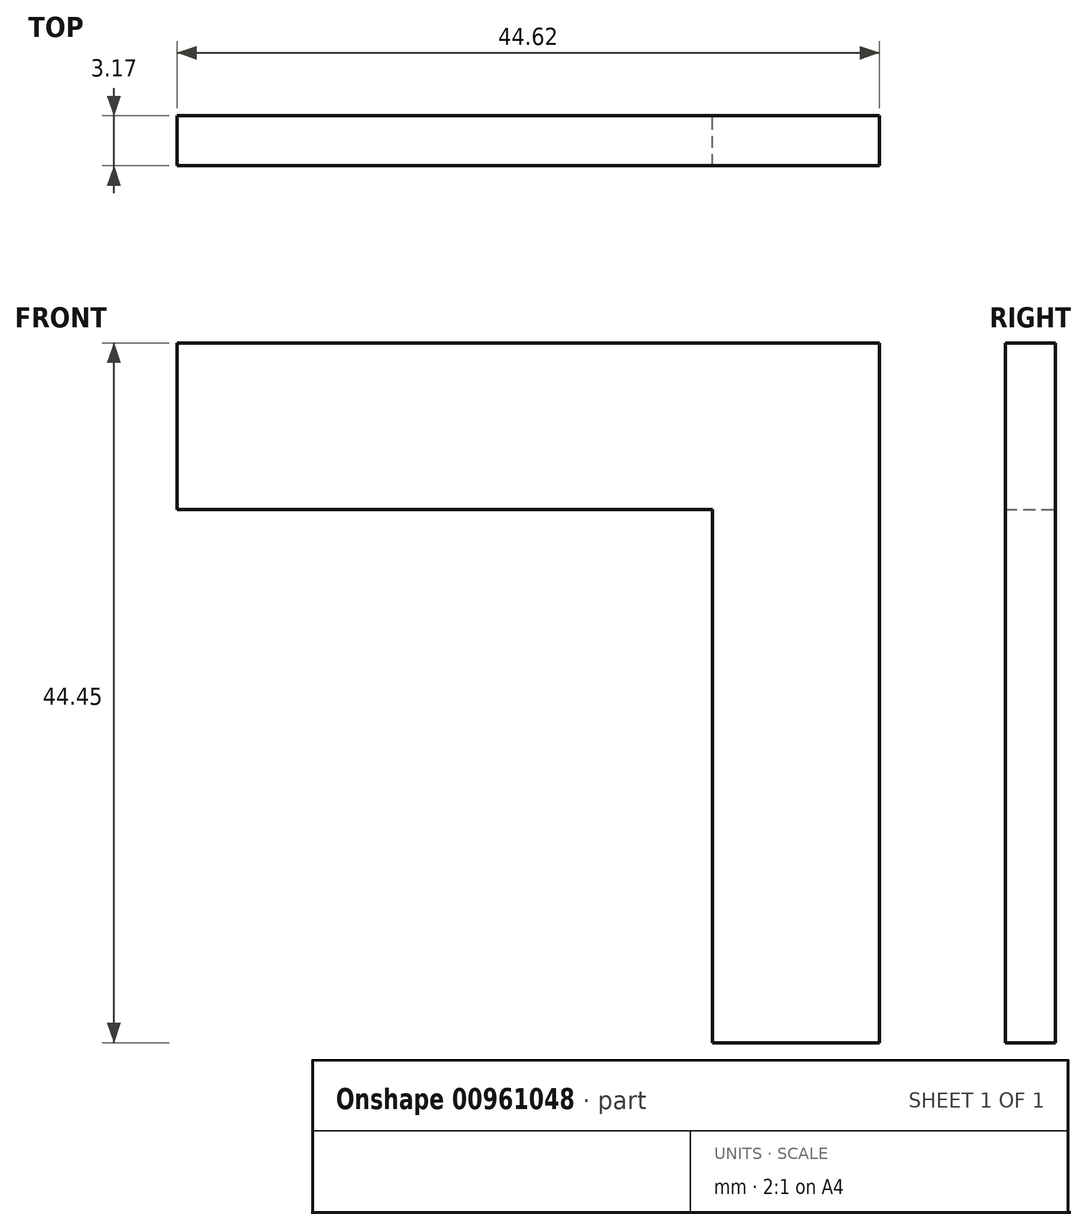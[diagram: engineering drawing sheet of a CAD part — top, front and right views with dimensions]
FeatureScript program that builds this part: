
annotation { "Feature Type Name" : "Feature", "Feature Type Description" : "" }
export const myFeature = defineFeature(function(context is Context, id is Id, definition is map)
    precondition{}
    {
        {
            var Q0;
            Q0=qCreatedBy(makeId("Front.planeOp"),FACE);
            var sketch = newSketch(context, id + "F0", { "sketchPlane" : qUnion([Q0])});
            skLineSegment(sketch, "E0", {"start": v(0, 0) * mm, "end": v(0, 33.85) * mm});
            skLineSegment(sketch, "E1", {"start": v(0, 33.85) * mm, "end": v(-34.02, 33.85) * mm});
            skLineSegment(sketch, "E2", {"start": v(-34.02, 33.85) * mm, "end": v(-34.02, 44.45) * mm});
            skLineSegment(sketch, "E3.0", {"start": v(10.6, 44.45) * mm, "end": v(-34.02, 44.45) * mm});
            skLineSegment(sketch, "E3.1", {"start": v(10.6, 0) * mm, "end": v(10.6, 44.45) * mm});
            skLineSegment(sketch, "E4", {"start": v(0, 0) * mm, "end": v(10.6, 0) * mm});
            skSolve(sketch);
        }
        {
            var Q0;
            Q0 = qSketchRegion(id + "F0", true);
            extrude(context, id + "F1", {"entities" : qUnion([Q0]), "depth" : 3.17 * mm, "offsetDistance" : 25 * mm});
        }
    });
